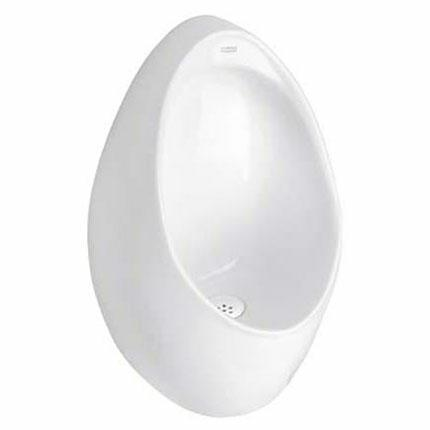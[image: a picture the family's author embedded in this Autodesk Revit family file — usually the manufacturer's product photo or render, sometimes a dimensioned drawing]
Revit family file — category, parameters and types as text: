
# Revit family: MG GOBI TDS
name_source: partatom
category: Plumbing Fixtures
units: mm (PartAtom-declared; Revit-internal decimal feet)

## family parameters
Always vertical = Yes
Cut with Voids When Loaded = No
OmniClass Number = 23.45.00.00
OmniClass Title = Sanitary, Laundry, and Cleaning Equipment
Part Type = Normal
Room Calculation Point = No
Round Connector Dimension = Use Diameter
Shared = No
Work Plane-Based = No

## types (1)
- MG GOBY TDS
    Ceramic = High Gloss Ceramic
    Certification = https://www.helvex.com.mx
    Default Elevation = 0"
    Description = MG GOBI TDS Dry Urinal
    Documentation = https://www.helvex.com.mx
    Features = Perfect Seal That Keeps Odor Away, Water Not Required, Easy Installation
    High Density Polypropylene = Polypropylene
    Inlet Threads = Flush: 1.5" (38 mm)
    Instructive = https://www.helvex.com.mx
    Manufacturer = Helvex
    Model = MG GOBI TDS
    Teflon Cartridge Base = Teflon
    Total Height = 25"
    Total Length = 16"
    Total Width = 11"
    Type Comments = Urinals
    Type Image = MG GOBI TDS.jpg
    URL = https://www.helvex.com.mx
    Waste Connection = Yes

## geometry (parser evidence)
native form markers: Sweep x2
no freeform markers — native parametric forms only
